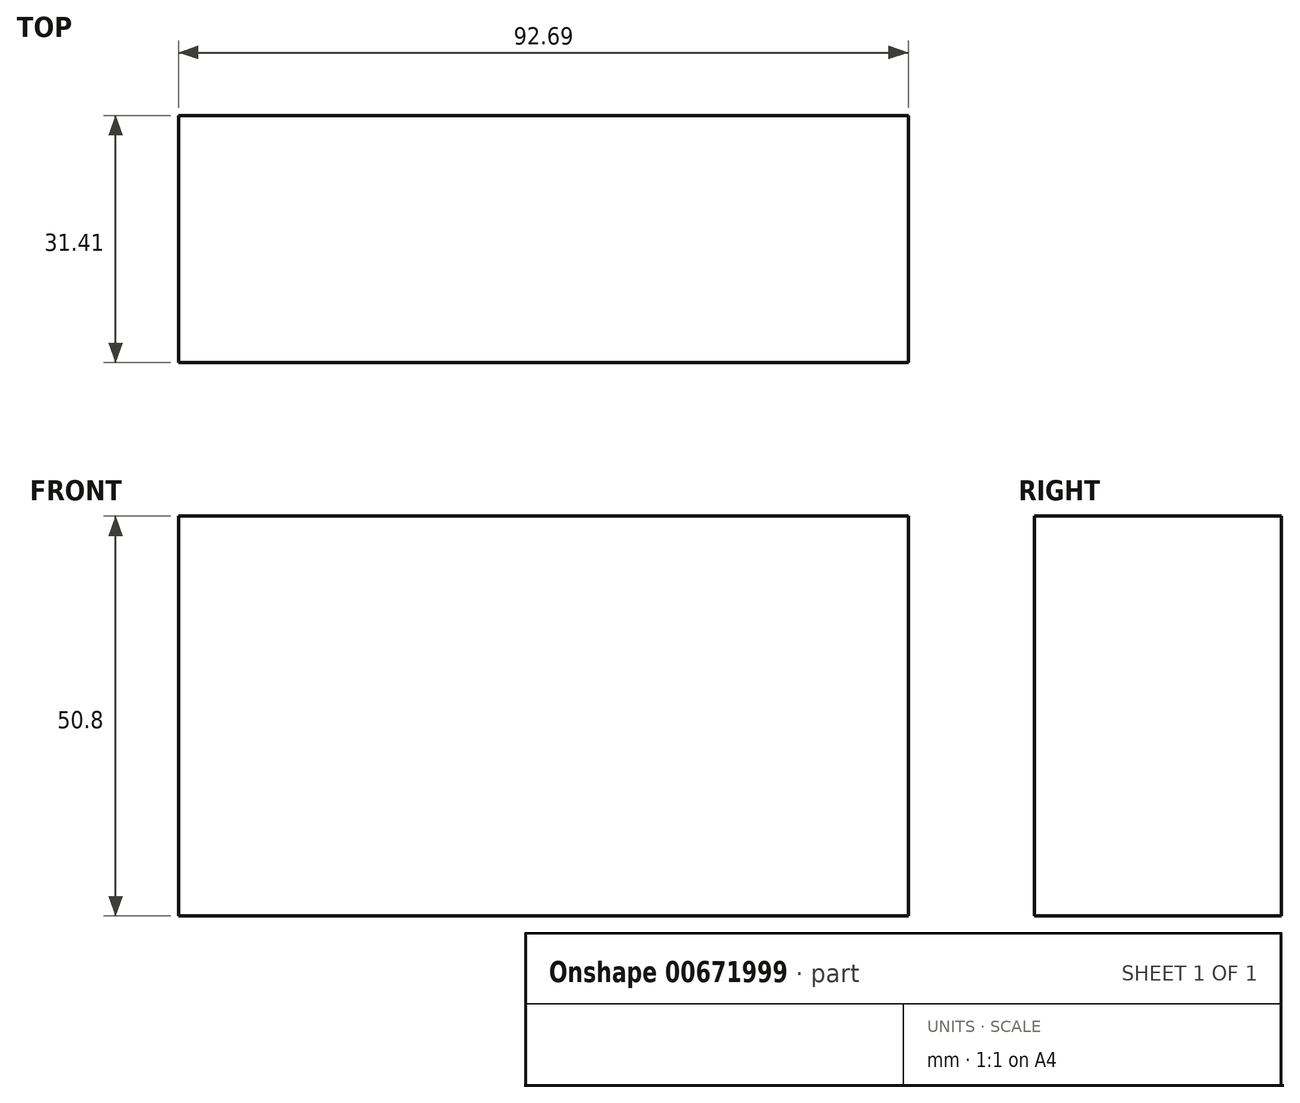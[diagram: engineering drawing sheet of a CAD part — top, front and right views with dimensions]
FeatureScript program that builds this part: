
annotation { "Feature Type Name" : "Feature", "Feature Type Description" : "" }
export const myFeature = defineFeature(function(context is Context, id is Id, definition is map)
    precondition{}
    {
        {
            var Q0;
            Q0=qCreatedBy(makeId("Top.planeOp"),FACE);
            var sketch = newSketch(context, id + "F0", { "sketchPlane" : qUnion([Q0])});
            skLineSegment(sketch, "E0.bottom", {"start": v(-60.31, -32.39) * mm, "end": v(32.38, -32.39) * mm});
            skLineSegment(sketch, "E0.top", {"start": v(-60.31, -63.8) * mm, "end": v(32.38, -63.8) * mm});
            skLineSegment(sketch, "E0.left", {"start": v(-60.31, -32.39) * mm, "end": v(-60.31, -63.8) * mm});
            skLineSegment(sketch, "E0.right", {"start": v(32.38, -32.39) * mm, "end": v(32.38, -63.8) * mm});
            skSolve(sketch);
        }
        {
            var Q0;
            Q0 = qSketchRegion(id + "F0", true);
            extrude(context, id + "F1", {"entities" : qUnion([Q0]), "depth" : 50.8 * mm, "offsetDistance" : 25.4 * mm});
        }
    });
